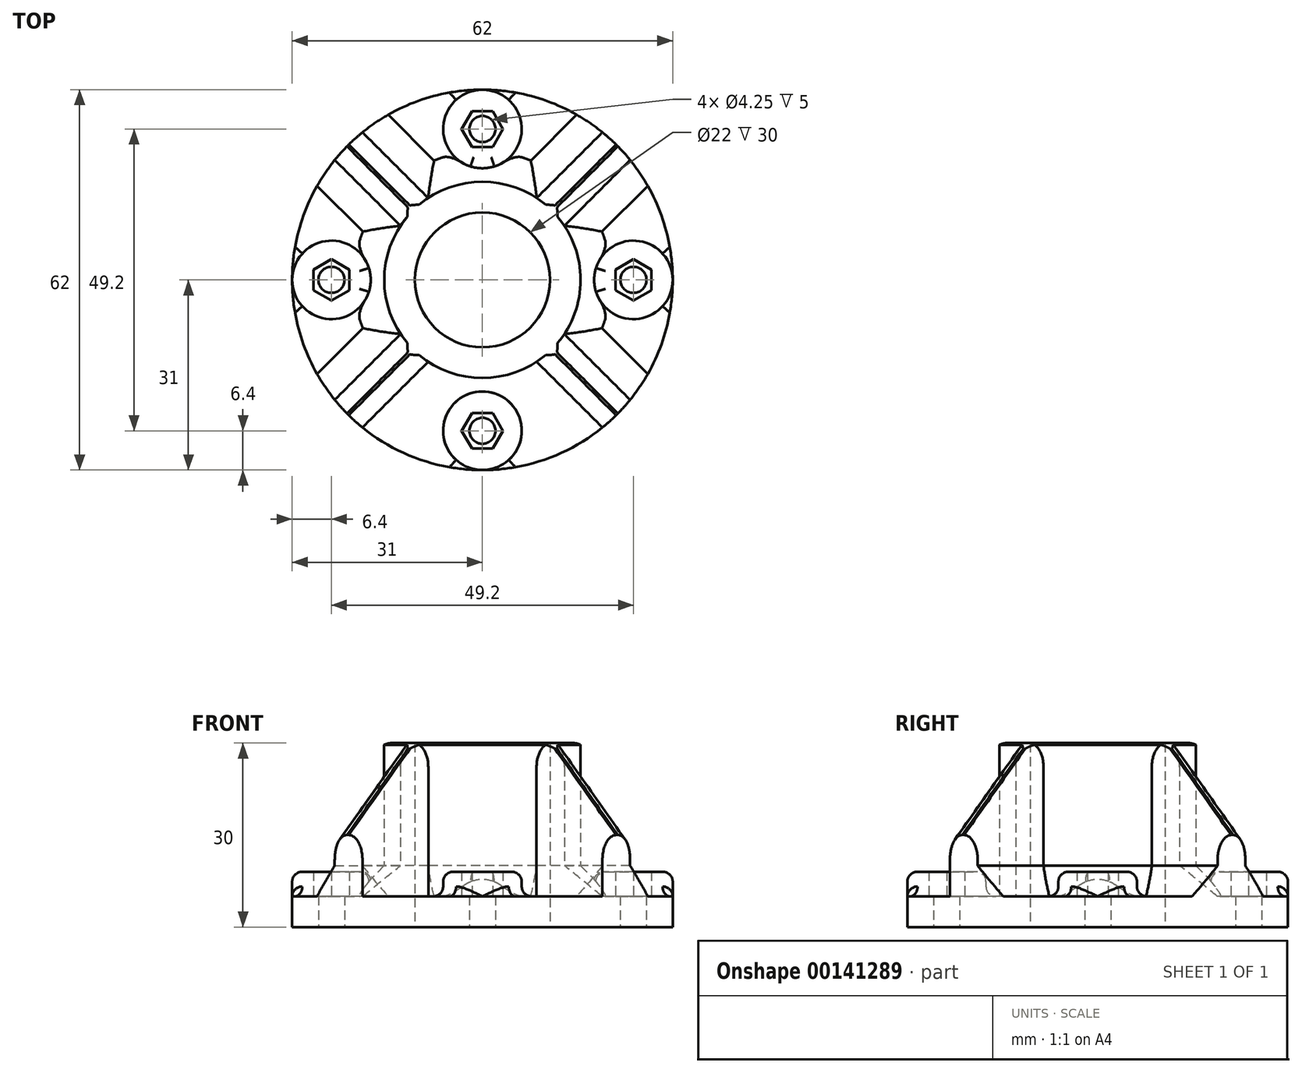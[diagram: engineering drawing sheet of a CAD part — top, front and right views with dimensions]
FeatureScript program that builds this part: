
annotation { "Feature Type Name" : "Feature", "Feature Type Description" : "" }
export const myFeature = defineFeature(function(context is Context, id is Id, definition is map)
    precondition{}
    {
        {
            var Q0;
            Q0=qCreatedBy(makeId("Top.planeOp"),FACE);
            var sketch = newSketch(context, id + "F0", { "sketchPlane" : qUnion([Q0])});
            skCircle(sketch, "E0", {"center": v(0, 0) * mm, "radius": 11 * mm});
            skCircle(sketch, "E1", {"center": v(0, 0) * mm, "radius": 31 * mm});
            skCircle(sketch, "E2", {"center": v(24.6, 0) * mm, "radius": 2.12 * mm});
            skCircle(sketch, "E3.1.0", {"center": v(0, 24.6) * mm, "radius": 2.12 * mm});
            skCircle(sketch, "E3.2.0", {"center": v(-24.6, 0) * mm, "radius": 2.12 * mm});
            skCircle(sketch, "E3.3.0", {"center": v(0, -24.6) * mm, "radius": 2.12 * mm});
            skSolve(sketch);
        }
        {
            var Q0;
            Q0=qSketchRegion(id+"F0",true);
            extrude(context, id + "F1", {"entities" : qUnion([Q0]), "depth" : 5 * mm});
        }
        {
            var Q0;
            Q0=makeQuery(id+"F1.opExtrude","CAP_FACE",FACE,{"disambiguationData":[OSD([sQuery(id+"F0.wireOp",EDGE,"E0"),sQuery(id+"F0.wireOp",EDGE,"E1")])],"isStart":false});
            var sketch = newSketch(context, id + "F2", { "sketchPlane" : qUnion([Q0])});
            skArc(sketch, "E4", {"start": v(-13.35, 8.83) * mm, "mid": v(-16, 0) * mm, "end": v(-13.35, -8.83) * mm});
            skCircle(sketch, "E5", {"center": v(0, 0) * mm, "radius": 11 * mm});
            skLineSegment(sketch, "E6", {"start": v(0, 0) * mm, "end": v(21.92, 21.92) * mm, "construction": true});
            skArc(sketch, "E7", {"start": v(19.54, 24.06) * mm, "mid": v(20.76, 23.02) * mm, "end": v(21.92, 21.92) * mm});
            skLineSegment(sketch, "E8", {"start": v(8.83, 13.35) * mm, "end": v(19.54, 24.06) * mm});
            skArc(sketch, "E9.MirrorCS", {"start": v(24.06, 19.54) * mm, "mid": v(23.02, 20.76) * mm, "end": v(21.92, 21.92) * mm});
            skLineSegment(sketch, "E10.MirrorCS", {"start": v(13.35, 8.83) * mm, "end": v(24.06, 19.54) * mm});
            skLineSegment(sketch, "E11.1.0", {"start": v(-13.35, 8.83) * mm, "end": v(-24.06, 19.54) * mm});
            skArc(sketch, "E11.1.1", {"start": v(-24.06, 19.54) * mm, "mid": v(-23.02, 20.76) * mm, "end": v(-21.92, 21.92) * mm});
            skArc(sketch, "E11.1.2", {"start": v(-19.54, 24.06) * mm, "mid": v(-20.76, 23.02) * mm, "end": v(-21.92, 21.92) * mm});
            skLineSegment(sketch, "E11.1.3", {"start": v(-8.83, 13.35) * mm, "end": v(-19.54, 24.06) * mm});
            skLineSegment(sketch, "E11.2.0", {"start": v(-8.83, -13.35) * mm, "end": v(-19.54, -24.06) * mm});
            skArc(sketch, "E11.2.1", {"start": v(-19.54, -24.06) * mm, "mid": v(-20.76, -23.02) * mm, "end": v(-21.92, -21.92) * mm});
            skArc(sketch, "E11.2.2", {"start": v(-24.06, -19.54) * mm, "mid": v(-23.02, -20.76) * mm, "end": v(-21.92, -21.92) * mm});
            skLineSegment(sketch, "E11.2.3", {"start": v(-13.35, -8.83) * mm, "end": v(-24.06, -19.54) * mm});
            skLineSegment(sketch, "E11.3.0", {"start": v(13.35, -8.83) * mm, "end": v(24.06, -19.54) * mm});
            skArc(sketch, "E11.3.1", {"start": v(24.06, -19.54) * mm, "mid": v(23.02, -20.76) * mm, "end": v(21.92, -21.92) * mm});
            skArc(sketch, "E11.3.2", {"start": v(19.54, -24.06) * mm, "mid": v(20.76, -23.02) * mm, "end": v(21.92, -21.92) * mm});
            skLineSegment(sketch, "E11.3.3", {"start": v(8.83, -13.35) * mm, "end": v(19.54, -24.06) * mm});
            skArc(sketch, "E12.trimOffspring", {"start": v(-8.83, -13.35) * mm, "mid": v(0, -16) * mm, "end": v(8.83, -13.35) * mm});
            skArc(sketch, "E13.trimOffspring", {"start": v(8.83, 13.35) * mm, "mid": v(0, 16) * mm, "end": v(-8.83, 13.35) * mm});
            skArc(sketch, "E14.trimOffspring", {"start": v(13.35, -8.83) * mm, "mid": v(16, 0) * mm, "end": v(13.35, 8.83) * mm});
            skSolve(sketch);
        }
        {
            var Q0;
            Q0=qSketchRegion(id+"F2",true);
            extrude(context, id + "F3", {"entities" : qUnion([Q0]), "operationType" : NewBodyOperationType.ADD, "depth" : 25 * mm});
        }
        {
            var Q0;
            Q0=makeQuery(id+"F3.opExtrude","CAP_EDGE",EDGE,{"disambiguationData":[OSD([sQuery(id+"F2.wireOp",EDGE,"E11.2.1"),sQuery(id+"F2.wireOp",EDGE,"E11.2.2")])],"isStart":false});
            var Q1;
            Q1=makeQuery(id+"F3.opExtrude","CAP_EDGE",EDGE,{"disambiguationData":[OSD([sQuery(id+"F2.wireOp",EDGE,"E11.3.1"),sQuery(id+"F2.wireOp",EDGE,"E11.3.2")])],"isStart":false});
            var Q2;
            Q2=makeQuery(id+"F3.opExtrude","CAP_EDGE",EDGE,{"disambiguationData":[OSD([sQuery(id+"F2.wireOp",EDGE,"E7"),sQuery(id+"F2.wireOp",EDGE,"E9.MirrorCS")])],"isStart":false});
            var Q3;
            Q3=makeQuery(id+"F3.opExtrude","CAP_EDGE",EDGE,{"disambiguationData":[OSD([sQuery(id+"F2.wireOp",EDGE,"E11.1.1"),sQuery(id+"F2.wireOp",EDGE,"E11.1.2")])],"isStart":false});
            chamfer(context, id + "F4", {"entities" : qUnion([Q0, Q1, Q2, Q3]), "width" : 15 * mm, "tangentPropagation" : true});
        }
        {
            var Q0;
            Q0=makeQuery(id+"F3.opExtrude","CAP_EDGE",EDGE,{"disambiguationData":[OSD([sQuery(id+"F2.wireOp",EDGE,"E12.trimOffspring")])],"isStart":true});
            var Q1;
            Q1=makeQuery(id+"F3.opExtrude","CAP_EDGE",EDGE,{"disambiguationData":[OSD([sQuery(id+"F2.wireOp",EDGE,"E11.3.3")])],"isStart":true});
            var Q2;
            Q2=makeQuery(id+"F3.opExtrude","CAP_EDGE",EDGE,{"disambiguationData":[OSD([sQuery(id+"F2.wireOp",EDGE,"E11.2.0")])],"isStart":true});
            var Q3;
            Q3=makeQuery(id+"F3.opExtrude","CAP_EDGE",EDGE,{"disambiguationData":[OSD([sQuery(id+"F2.wireOp",EDGE,"E14.trimOffspring")])],"isStart":true});
            var Q4;
            Q4=makeQuery(id+"F3.opExtrude","CAP_EDGE",EDGE,{"disambiguationData":[OSD([sQuery(id+"F2.wireOp",EDGE,"E10.MirrorCS")])],"isStart":true});
            var Q5;
            Q5=makeQuery(id+"F3.opExtrude","CAP_EDGE",EDGE,{"disambiguationData":[OSD([sQuery(id+"F2.wireOp",EDGE,"E11.3.0")])],"isStart":true});
            var Q6;
            Q6=makeQuery(id+"F3.opExtrude","CAP_EDGE",EDGE,{"disambiguationData":[OSD([sQuery(id+"F2.wireOp",EDGE,"E13.trimOffspring")])],"isStart":true});
            var Q7;
            Q7=makeQuery(id+"F3.opExtrude","CAP_EDGE",EDGE,{"disambiguationData":[OSD([sQuery(id+"F2.wireOp",EDGE,"E11.1.3")])],"isStart":true});
            var Q8;
            Q8=makeQuery(id+"F3.opExtrude","CAP_EDGE",EDGE,{"disambiguationData":[OSD([sQuery(id+"F2.wireOp",EDGE,"E8")])],"isStart":true});
            var Q9;
            Q9=makeQuery(id+"F3.opExtrude","CAP_EDGE",EDGE,{"disambiguationData":[OSD([sQuery(id+"F2.wireOp",EDGE,"E4")])],"isStart":true});
            var Q10;
            Q10=makeQuery(id+"F3.opExtrude","CAP_EDGE",EDGE,{"disambiguationData":[OSD([sQuery(id+"F2.wireOp",EDGE,"E11.1.0")])],"isStart":true});
            var Q11;
            Q11=makeQuery(id+"F3.opExtrude","CAP_EDGE",EDGE,{"disambiguationData":[OSD([sQuery(id+"F2.wireOp",EDGE,"E11.2.3")])],"isStart":true});
            chamfer(context, id + "F5", {"entities" : qUnion([Q0, Q1, Q2, Q3, Q4, Q5, Q6, Q7, Q8, Q9, Q10, Q11]), "width" : 5 * mm, "tangentPropagation" : true});
        }
        {
            var Q0;
            Q0=makeQuery(id+"F4.opChamfer","BLEND_EDGE",EDGE,{"blendedFrom":[makeQuery(id+"F3.opExtrude","CAP_EDGE",EDGE,{"disambiguationData":[OSD([sQuery(id+"F2.wireOp",EDGE,"E11.2.1"),sQuery(id+"F2.wireOp",EDGE,"E11.2.2")])],"isStart":false}),makeQuery(id+"F3.opExtrude","SWEPT_FACE",FACE,{"disambiguationData":[OSD([sQuery(id+"F2.wireOp",EDGE,"E11.2.3")])]})],"blendedInto":[makeQuery(id+"F3.opExtrude","SWEPT_FACE",FACE,{"disambiguationData":[OSD([sQuery(id+"F2.wireOp",EDGE,"E11.2.3")])]})]});
            var Q1;
            Q1=makeQuery(id+"F4.opChamfer","BLEND_EDGE",EDGE,{"blendedFrom":[makeQuery(id+"F3.opExtrude","CAP_EDGE",EDGE,{"disambiguationData":[OSD([sQuery(id+"F2.wireOp",EDGE,"E11.2.1"),sQuery(id+"F2.wireOp",EDGE,"E11.2.2")])],"isStart":false}),makeQuery(id+"F3.opExtrude","SWEPT_FACE",FACE,{"disambiguationData":[OSD([sQuery(id+"F2.wireOp",EDGE,"E11.2.0")])]})],"blendedInto":[makeQuery(id+"F3.opExtrude","SWEPT_FACE",FACE,{"disambiguationData":[OSD([sQuery(id+"F2.wireOp",EDGE,"E11.2.0")])]})]});
            var Q2;
            Q2=makeQuery(id+"F4.opChamfer","BLEND_EDGE",EDGE,{"blendedFrom":[makeQuery(id+"F3.opExtrude","CAP_EDGE",EDGE,{"disambiguationData":[OSD([sQuery(id+"F2.wireOp",EDGE,"E11.3.1"),sQuery(id+"F2.wireOp",EDGE,"E11.3.2")])],"isStart":false}),makeQuery(id+"F3.opExtrude","SWEPT_FACE",FACE,{"disambiguationData":[OSD([sQuery(id+"F2.wireOp",EDGE,"E11.3.3")])]})],"blendedInto":[makeQuery(id+"F3.opExtrude","SWEPT_FACE",FACE,{"disambiguationData":[OSD([sQuery(id+"F2.wireOp",EDGE,"E11.3.3")])]})]});
            var Q3;
            Q3=makeQuery(id+"F4.opChamfer","BLEND_EDGE",EDGE,{"blendedFrom":[makeQuery(id+"F3.opExtrude","CAP_EDGE",EDGE,{"disambiguationData":[OSD([sQuery(id+"F2.wireOp",EDGE,"E11.3.1"),sQuery(id+"F2.wireOp",EDGE,"E11.3.2")])],"isStart":false}),makeQuery(id+"F3.opExtrude","SWEPT_FACE",FACE,{"disambiguationData":[OSD([sQuery(id+"F2.wireOp",EDGE,"E11.3.0")])]})],"blendedInto":[makeQuery(id+"F3.opExtrude","SWEPT_FACE",FACE,{"disambiguationData":[OSD([sQuery(id+"F2.wireOp",EDGE,"E11.3.0")])]})]});
            var Q4;
            Q4=makeQuery(id+"F4.opChamfer","BLEND_EDGE",EDGE,{"blendedFrom":[makeQuery(id+"F3.opExtrude","CAP_EDGE",EDGE,{"disambiguationData":[OSD([sQuery(id+"F2.wireOp",EDGE,"E7"),sQuery(id+"F2.wireOp",EDGE,"E9.MirrorCS")])],"isStart":false}),makeQuery(id+"F3.opExtrude","SWEPT_FACE",FACE,{"disambiguationData":[OSD([sQuery(id+"F2.wireOp",EDGE,"E10.MirrorCS")])]})],"blendedInto":[makeQuery(id+"F3.opExtrude","SWEPT_FACE",FACE,{"disambiguationData":[OSD([sQuery(id+"F2.wireOp",EDGE,"E10.MirrorCS")])]})]});
            var Q5;
            Q5=makeQuery(id+"F4.opChamfer","BLEND_EDGE",EDGE,{"blendedFrom":[makeQuery(id+"F3.opExtrude","CAP_EDGE",EDGE,{"disambiguationData":[OSD([sQuery(id+"F2.wireOp",EDGE,"E7"),sQuery(id+"F2.wireOp",EDGE,"E9.MirrorCS")])],"isStart":false}),makeQuery(id+"F3.opExtrude","SWEPT_FACE",FACE,{"disambiguationData":[OSD([sQuery(id+"F2.wireOp",EDGE,"E8")])]})],"blendedInto":[makeQuery(id+"F3.opExtrude","SWEPT_FACE",FACE,{"disambiguationData":[OSD([sQuery(id+"F2.wireOp",EDGE,"E8")])]})]});
            var Q6;
            Q6=makeQuery(id+"F4.opChamfer","BLEND_EDGE",EDGE,{"blendedFrom":[makeQuery(id+"F3.opExtrude","CAP_EDGE",EDGE,{"disambiguationData":[OSD([sQuery(id+"F2.wireOp",EDGE,"E11.1.1"),sQuery(id+"F2.wireOp",EDGE,"E11.1.2")])],"isStart":false}),makeQuery(id+"F3.opExtrude","SWEPT_FACE",FACE,{"disambiguationData":[OSD([sQuery(id+"F2.wireOp",EDGE,"E11.1.3")])]})],"blendedInto":[makeQuery(id+"F3.opExtrude","SWEPT_FACE",FACE,{"disambiguationData":[OSD([sQuery(id+"F2.wireOp",EDGE,"E11.1.3")])]})]});
            var Q7;
            Q7=makeQuery(id+"F4.opChamfer","BLEND_EDGE",EDGE,{"blendedFrom":[makeQuery(id+"F3.opExtrude","CAP_EDGE",EDGE,{"disambiguationData":[OSD([sQuery(id+"F2.wireOp",EDGE,"E11.1.1"),sQuery(id+"F2.wireOp",EDGE,"E11.1.2")])],"isStart":false}),makeQuery(id+"F3.opExtrude","SWEPT_FACE",FACE,{"disambiguationData":[OSD([sQuery(id+"F2.wireOp",EDGE,"E11.1.0")])]})],"blendedInto":[makeQuery(id+"F3.opExtrude","SWEPT_FACE",FACE,{"disambiguationData":[OSD([sQuery(id+"F2.wireOp",EDGE,"E11.1.0")])]})]});
            fillet(context, id + "F6", {"entities" : qUnion([Q0, Q1, Q2, Q3, Q4, Q5, Q6, Q7]), "radius" : 3 * mm, "tangentPropagation" : true, "allowEdgeOverflow" : false});
        }
        {
            var Q0;
            Q0=makeQuery(id+"F3.opExtrude","CAP_EDGE",EDGE,{"disambiguationData":[OSD([sQuery(id+"F2.wireOp",EDGE,"E12.trimOffspring")])],"isStart":false});
            var Q1;
            Q1=makeQuery(id+"F3.opExtrude","CAP_EDGE",EDGE,{"disambiguationData":[OSD([sQuery(id+"F2.wireOp",EDGE,"E14.trimOffspring")])],"isStart":false});
            var Q2;
            Q2=makeQuery(id+"F3.opExtrude","CAP_EDGE",EDGE,{"disambiguationData":[OSD([sQuery(id+"F2.wireOp",EDGE,"E13.trimOffspring")])],"isStart":false});
            var Q3;
            Q3=makeQuery(id+"F3.opExtrude","CAP_EDGE",EDGE,{"disambiguationData":[OSD([sQuery(id+"F2.wireOp",EDGE,"E4")])],"isStart":false});
            fillet(context, id + "F7", {"entities" : qUnion([Q0, Q1, Q2, Q3]), "radius" : 3.2 * mm, "tangentPropagation" : true, "allowEdgeOverflow" : false});
        }
        {
            var Q0;
            {var subQ0=sQuery(id+"F0.wireOp",EDGE,"E3.1.0");var subQ1=sQuery(id+"F0.wireOp",EDGE,"E1");Q0=makeQuery(id+"F3.boolean.opBoolean","SPLIT",FACE,{"disambiguationData":[TD([makeQuery(id+"F1.opExtrude","SWEPT_FACE",FACE,{"disambiguationData":[OSD([subQ0])]})])],"derivedFrom":makeQuery(id+"F1.opExtrude","CAP_FACE",FACE,{"disambiguationData":[OSD([sQuery(id+"F0.wireOp",EDGE,"E0"),subQ1,sQuery(id+"F0.wireOp",EDGE,"E2"),subQ0,sQuery(id+"F0.wireOp",EDGE,"E3.2.0"),sQuery(id+"F0.wireOp",EDGE,"E3.3.0")])],"isStart":false})});}
            var sketch = newSketch(context, id + "F8", { "sketchPlane" : qUnion([Q0])});
            skCircle(sketch, "E15.cCircle", {"center": v(24.6, 0) * mm, "radius": 2.91 * mm, "construction": true});
            skLineSegment(sketch, "E15.0", {"start": v(27.51, 1.68) * mm, "end": v(27.51, -1.68) * mm});
            skLineSegment(sketch, "E15.1", {"start": v(27.51, -1.68) * mm, "end": v(24.6, -3.36) * mm});
            skLineSegment(sketch, "E15.2", {"start": v(24.6, -3.36) * mm, "end": v(21.69, -1.68) * mm});
            skLineSegment(sketch, "E15.3", {"start": v(21.69, -1.68) * mm, "end": v(21.69, 1.68) * mm});
            skLineSegment(sketch, "E15.4", {"start": v(21.69, 1.68) * mm, "end": v(24.6, 3.36) * mm});
            skLineSegment(sketch, "E15.5", {"start": v(24.6, 3.36) * mm, "end": v(27.51, 1.68) * mm});
            skPoint(sketch, "E15.0.midPoint", {"position": v(27.51, 0) * mm});
            skCircle(sketch, "E16", {"center": v(24.6, 0) * mm, "radius": 6.4 * mm});
            skCircle(sketch, "E17.1.0", {"center": v(0, 24.6) * mm, "radius": 6.4 * mm});
            skLineSegment(sketch, "E17.1.1", {"start": v(-3.36, 24.6) * mm, "end": v(-1.68, 27.51) * mm});
            skLineSegment(sketch, "E17.1.2", {"start": v(1.68, 27.51) * mm, "end": v(3.36, 24.6) * mm});
            skCircle(sketch, "E17.1.3", {"center": v(0, 24.6) * mm, "radius": 2.91 * mm, "construction": true});
            skPoint(sketch, "E17.1.4", {"position": v(0, 27.51) * mm});
            skLineSegment(sketch, "E17.1.5", {"start": v(-1.68, 21.69) * mm, "end": v(-3.36, 24.6) * mm});
            skLineSegment(sketch, "E17.1.6", {"start": v(1.68, 21.69) * mm, "end": v(-1.68, 21.69) * mm});
            skLineSegment(sketch, "E17.1.7", {"start": v(3.36, 24.6) * mm, "end": v(1.68, 21.69) * mm});
            skLineSegment(sketch, "E17.1.8", {"start": v(-1.68, 27.51) * mm, "end": v(1.68, 27.51) * mm});
            skCircle(sketch, "E17.2.0", {"center": v(-24.6, 0) * mm, "radius": 6.4 * mm});
            skLineSegment(sketch, "E17.2.1", {"start": v(-24.6, -3.36) * mm, "end": v(-27.51, -1.68) * mm});
            skLineSegment(sketch, "E17.2.2", {"start": v(-27.51, 1.68) * mm, "end": v(-24.6, 3.36) * mm});
            skCircle(sketch, "E17.2.3", {"center": v(-24.6, 0) * mm, "radius": 2.91 * mm, "construction": true});
            skPoint(sketch, "E17.2.4", {"position": v(-27.51, 0) * mm});
            skLineSegment(sketch, "E17.2.5", {"start": v(-21.69, -1.68) * mm, "end": v(-24.6, -3.36) * mm});
            skLineSegment(sketch, "E17.2.6", {"start": v(-21.69, 1.68) * mm, "end": v(-21.69, -1.68) * mm});
            skLineSegment(sketch, "E17.2.7", {"start": v(-24.6, 3.36) * mm, "end": v(-21.69, 1.68) * mm});
            skLineSegment(sketch, "E17.2.8", {"start": v(-27.51, -1.68) * mm, "end": v(-27.51, 1.68) * mm});
            skCircle(sketch, "E17.3.0", {"center": v(0, -24.6) * mm, "radius": 6.4 * mm});
            skLineSegment(sketch, "E17.3.1", {"start": v(3.36, -24.6) * mm, "end": v(1.68, -27.51) * mm});
            skLineSegment(sketch, "E17.3.2", {"start": v(-1.68, -27.51) * mm, "end": v(-3.36, -24.6) * mm});
            skCircle(sketch, "E17.3.3", {"center": v(0, -24.6) * mm, "radius": 2.91 * mm, "construction": true});
            skPoint(sketch, "E17.3.4", {"position": v(0, -27.51) * mm});
            skLineSegment(sketch, "E17.3.5", {"start": v(1.68, -21.69) * mm, "end": v(3.36, -24.6) * mm});
            skLineSegment(sketch, "E17.3.6", {"start": v(-1.68, -21.69) * mm, "end": v(1.68, -21.69) * mm});
            skLineSegment(sketch, "E17.3.7", {"start": v(-3.36, -24.6) * mm, "end": v(-1.68, -21.69) * mm});
            skLineSegment(sketch, "E17.3.8", {"start": v(1.68, -27.51) * mm, "end": v(-1.68, -27.51) * mm});
            skPoint(sketch, "E17.center", {"position": v(0, 0) * mm});
            skSolve(sketch);
        }
        {
            var Q0;
            Q0 = qSketchRegion(id + "F8", true);
            extrude(context, id + "F9", {"entities" : qUnion([Q0]), "operationType" : NewBodyOperationType.ADD, "depth" : 4 * mm});
        }
        {
            var Q0;
            Q0=makeQuery(id+"F9.boolean.opBoolean","SPLIT",EDGE,{"disambiguationData":[OD(1.0)],"derivedFrom":makeQuery(id+"F9.opExtrude","CAP_EDGE",EDGE,{"disambiguationData":[OSD([sQuery(id+"F8.wireOp",EDGE,"E16")])],"isStart":true})});
            var Q1;
            Q1=makeQuery(id+"F9.boolean.opBoolean","SPLIT",EDGE,{"disambiguationData":[OD(1.0)],"derivedFrom":makeQuery(id+"F9.opExtrude","CAP_EDGE",EDGE,{"disambiguationData":[OSD([sQuery(id+"F8.wireOp",EDGE,"E17.3.0")])],"isStart":true})});
            var Q2;
            Q2=makeQuery(id+"F9.boolean.opBoolean","SPLIT",EDGE,{"disambiguationData":[OD(1.0)],"derivedFrom":makeQuery(id+"F9.opExtrude","CAP_EDGE",EDGE,{"disambiguationData":[OSD([sQuery(id+"F8.wireOp",EDGE,"E17.2.0")])],"isStart":true})});
            var Q3;
            Q3=makeQuery(id+"F9.opExtrude","CAP_EDGE",EDGE,{"disambiguationData":[OSD([sQuery(id+"F8.wireOp",EDGE,"E17.2.0")])],"isStart":false});
            var Q4;
            Q4=makeQuery(id+"F9.opExtrude","CAP_EDGE",EDGE,{"disambiguationData":[OSD([sQuery(id+"F8.wireOp",EDGE,"E17.3.0")])],"isStart":false});
            var Q5;
            Q5=makeQuery(id+"F9.opExtrude","CAP_EDGE",EDGE,{"disambiguationData":[OSD([sQuery(id+"F8.wireOp",EDGE,"E16")])],"isStart":false});
            var Q6;
            Q6=makeQuery(id+"F9.opExtrude","CAP_EDGE",EDGE,{"disambiguationData":[OSD([sQuery(id+"F8.wireOp",EDGE,"E17.1.0")])],"isStart":false});
            var Q7;
            Q7=makeQuery(id+"F9.boolean.opBoolean","SPLIT",EDGE,{"disambiguationData":[OD(1.0)],"derivedFrom":makeQuery(id+"F9.opExtrude","CAP_EDGE",EDGE,{"disambiguationData":[OSD([sQuery(id+"F8.wireOp",EDGE,"E17.1.0")])],"isStart":true})});
            fillet(context, id + "F10", {"entities" : qUnion([Q0, Q1, Q2, Q3, Q4, Q5, Q6, Q7]), "radius" : 1.6 * mm, "tangentPropagation" : true, "allowEdgeOverflow" : false});
        }
    });
